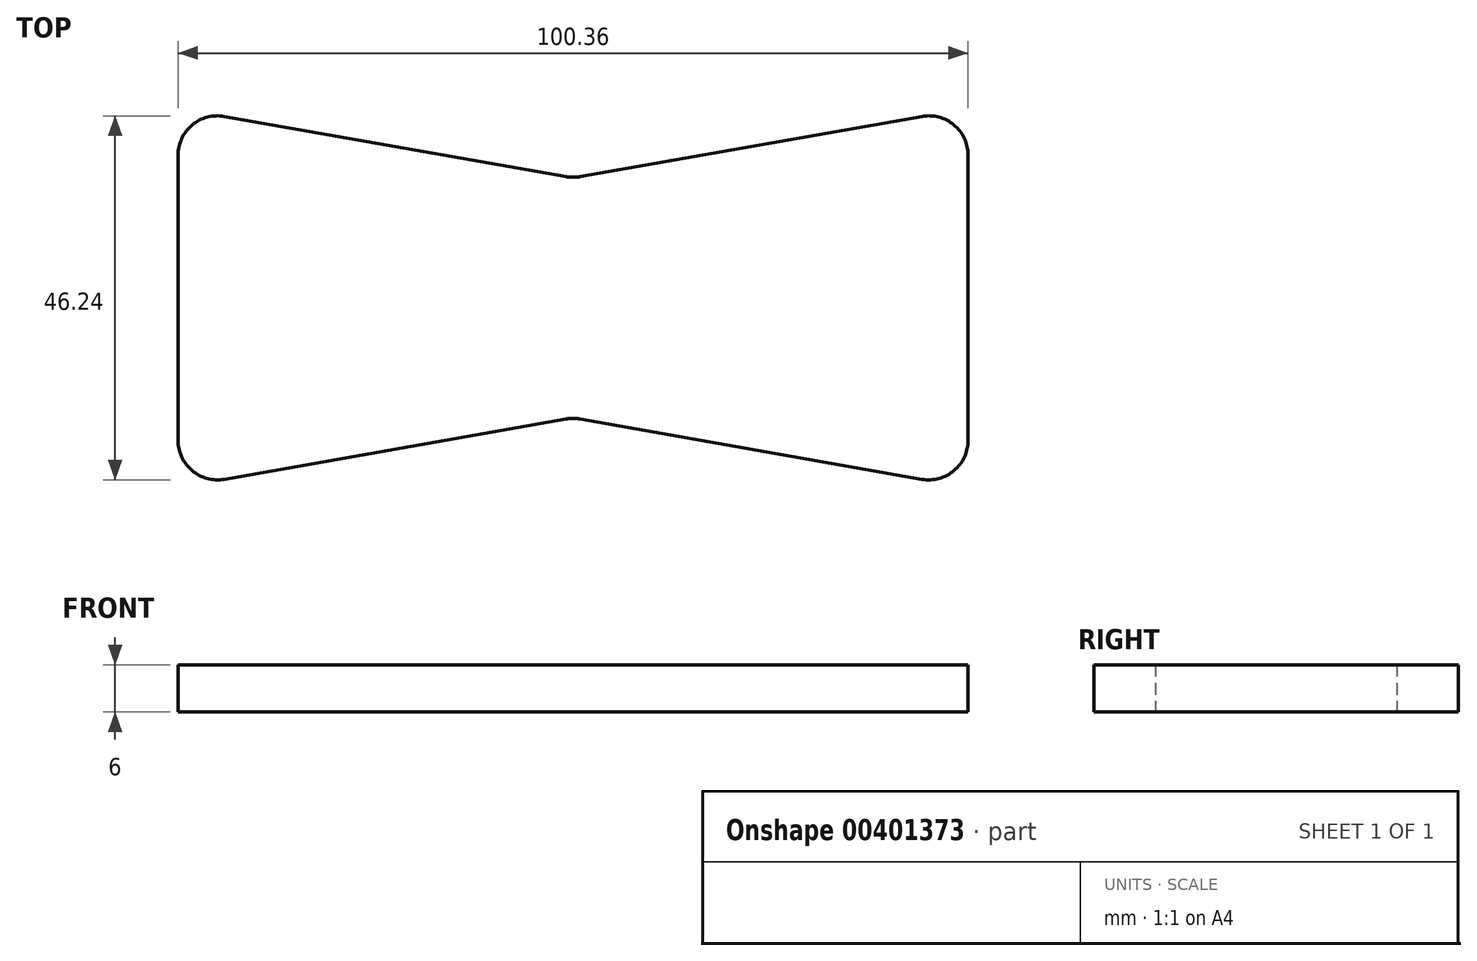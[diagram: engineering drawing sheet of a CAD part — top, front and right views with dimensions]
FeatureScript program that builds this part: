
annotation { "Feature Type Name" : "Feature", "Feature Type Description" : "" }
export const myFeature = defineFeature(function(context is Context, id is Id, definition is map)
    precondition{}
    {
        {
            var Q0;
            Q0=qCreatedBy(makeId("Top.planeOp"),FACE);
            var sketch = newSketch(context, id + "F0", { "sketchPlane" : qUnion([Q0])});
            skLineSegment(sketch, "E0", {"start": v(0, 0) * mm, "end": v(0, 30.93) * mm, "construction": true});
            skLineSegment(sketch, "E1", {"start": v(0, 0) * mm, "end": v(0, -30) * mm, "construction": true});
            skLineSegment(sketch, "E2", {"start": v(0.87, 15.62) * mm, "end": v(44.3, 23.28) * mm});
            skLineSegment(sketch, "E3", {"start": v(50.18, 18.35) * mm, "end": v(50.18, -17.89) * mm});
            skLineSegment(sketch, "E4", {"start": v(44.3, -22.81) * mm, "end": v(0.87, -15.15) * mm});
            skLineSegment(sketch, "E5", {"start": v(-0.87, -15.15) * mm, "end": v(-44.3, -22.81) * mm});
            skLineSegment(sketch, "E6", {"start": v(-50.18, -17.89) * mm, "end": v(-50.18, 18.35) * mm});
            skLineSegment(sketch, "E7", {"start": v(-44.3, 23.28) * mm, "end": v(-0.87, 15.62) * mm});
            skPoint(sketch, "E8.visualSharp", {"position": v(50.18, 24.31) * mm});
            skArc(sketch, "E8.filletArc", {"start": v(50.18, 18.35) * mm, "mid": v(48.4, 22.18) * mm, "end": v(44.3, 23.28) * mm});
            skPoint(sketch, "E9.visualSharp", {"position": v(50.18, -23.85) * mm});
            skArc(sketch, "E9.filletArc", {"start": v(44.3, -22.81) * mm, "mid": v(48.4, -21.72) * mm, "end": v(50.18, -17.89) * mm});
            skPoint(sketch, "E10.visualSharp", {"position": v(-50.18, -23.85) * mm});
            skArc(sketch, "E10.filletArc", {"start": v(-50.18, -17.89) * mm, "mid": v(-48.4, -21.72) * mm, "end": v(-44.3, -22.81) * mm});
            skPoint(sketch, "E11.visualSharp", {"position": v(-50.18, 24.31) * mm});
            skArc(sketch, "E11.filletArc", {"start": v(-44.3, 23.28) * mm, "mid": v(-48.4, 22.18) * mm, "end": v(-50.18, 18.35) * mm});
            skPoint(sketch, "E12.visualSharp", {"position": v(0, 15.46) * mm});
            skArc(sketch, "E12.filletArc", {"start": v(-0.87, 15.62) * mm, "mid": v(0, 15.54) * mm, "end": v(0.87, 15.62) * mm});
            skPoint(sketch, "E13.visualSharp", {"position": v(0, -15) * mm});
            skArc(sketch, "E13.filletArc", {"start": v(0.87, -15.15) * mm, "mid": v(0, -15.08) * mm, "end": v(-0.87, -15.15) * mm});
            skSolve(sketch);
        }
        {
            var Q0;
            Q0=makeQuery(id+"F0.imprint","IMPRINT",FACE,{"disambiguationData":[TD([[makeQuery(id+"F0.imprint","IMPRINT",EDGE,{"derivedFrom":sQuery(id+"F0.wireOp",EDGE,"E2")}),-1.0]])]});
            extrude(context, id + "F1", {"entities" : qUnion([Q0]), "depth" : 6 * mm, "offsetDistance" : 25 * mm});
        }
    });
